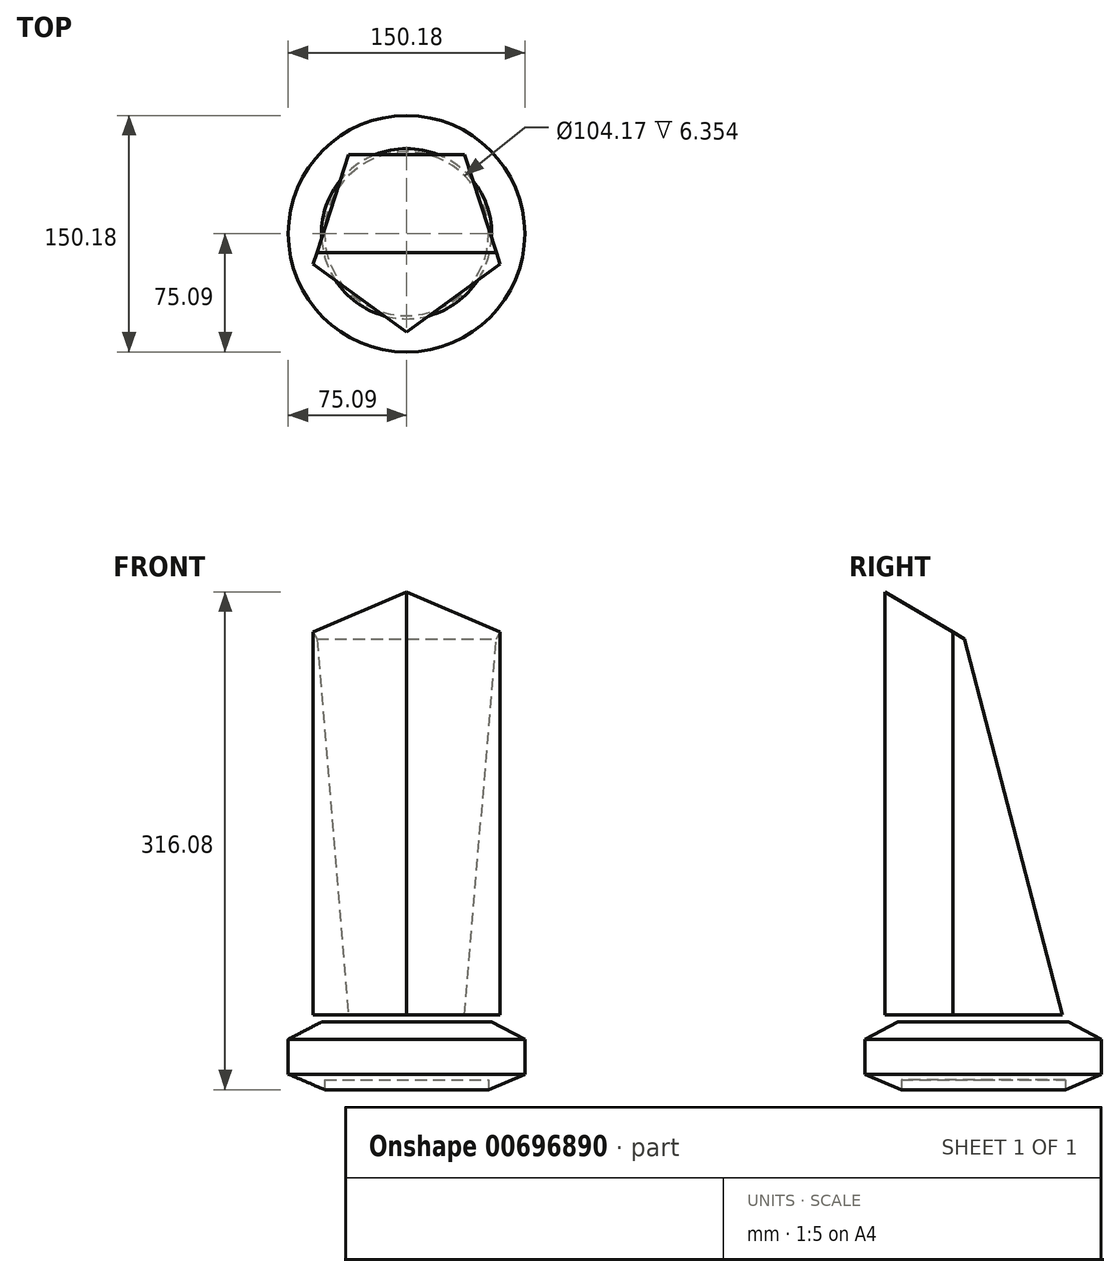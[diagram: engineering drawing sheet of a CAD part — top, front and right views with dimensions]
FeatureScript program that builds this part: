
annotation { "Feature Type Name" : "Feature", "Feature Type Description" : "" }
export const myFeature = defineFeature(function(context is Context, id is Id, definition is map)
    precondition{}
    {
        {
            var Q0;
            Q0=qCreatedBy(makeId("Top.planeOp"),FACE);
            var sketch = newSketch(context, id + "F0", { "sketchPlane" : qUnion([Q0])});
            skCircle(sketch, "E0.cCircle", {"center": v(0, 0) * mm, "radius": 50.53 * mm, "construction": true});
            skLineSegment(sketch, "E0.0", {"start": v(-36.71, 50.53) * mm, "end": v(36.71, 50.53) * mm});
            skLineSegment(sketch, "E0.1", {"start": v(36.71, 50.53) * mm, "end": v(59.4, -19.3) * mm});
            skLineSegment(sketch, "E0.2", {"start": v(59.4, -19.3) * mm, "end": v(0, -62.46) * mm});
            skLineSegment(sketch, "E0.3", {"start": v(0, -62.46) * mm, "end": v(-59.4, -19.3) * mm});
            skLineSegment(sketch, "E0.4", {"start": v(-59.4, -19.3) * mm, "end": v(-36.71, 50.53) * mm});
            skPoint(sketch, "E0.0.midPoint", {"position": v(0, 50.53) * mm});
            skSolve(sketch);
        }
        {
            var Q0;
            Q0=makeQuery(id+"F0.imprint","IMPRINT",FACE,{"disambiguationData":[TD([[makeQuery(id+"F0.imprint","IMPRINT",EDGE,{"derivedFrom":sQuery(id+"F0.wireOp",EDGE,"E0.0")}),-1.0]])]});
            extrude(context, id + "F1", {"entities" : qUnion([Q0]), "depth" : 274.32 * mm, "offsetDistance" : 25.4 * mm});
        }
        {
            var Q0;
            Q0=qCreatedBy(makeId("Right.planeOp"),FACE);
            var sketch = newSketch(context, id + "F2", { "sketchPlane" : qUnion([Q0])});
            skLineSegment(sketch, "E1", {"start": v(110.7, 303.13) * mm, "end": v(53.46, -12.62) * mm});
            skLineSegment(sketch, "E2", {"start": v(53.46, -12.62) * mm, "end": v(-11.84, 238.66) * mm});
            skLineSegment(sketch, "E3", {"start": v(-11.84, 238.66) * mm, "end": v(-68.95, 272.35) * mm});
            skLineSegment(sketch, "E4", {"start": v(-68.95, 272.35) * mm, "end": v(-68.95, 303.13) * mm});
            skLineSegment(sketch, "E5", {"start": v(-68.95, 303.13) * mm, "end": v(110.7, 303.13) * mm});
            skSolve(sketch);
        }
        {
            var Q0;
            Q0 = qSketchRegion(id + "F2", true);
            extrude(context, id + "F3", {"entities" : qUnion([Q0]), "operationType" : NewBodyOperationType.REMOVE, "oppositeDirection" : true, "depth" : 76.2 * mm, "offsetDistance" : 25.4 * mm, "hasSecondDirection" : true, "secondDirectionOppositeDirection" : false, "secondDirectionDepth" : 76.2 * mm});
        }
        {
            var Q0;
            Q0=qCreatedBy(makeId("Front.planeOp"),FACE);
            var sketch = newSketch(context, id + "F4", { "sketchPlane" : qUnion([Q0])});
            skLineSegment(sketch, "E6", {"start": v(0, -29.8) * mm, "end": v(0, -4.6) * mm, "construction": true});
            skLineSegment(sketch, "E7", {"start": v(0, -4.6) * mm, "end": v(-54.06, -4.6) * mm});
            skLineSegment(sketch, "E8", {"start": v(-54.06, -4.6) * mm, "end": v(-75.1, -15.56) * mm});
            skLineSegment(sketch, "E9", {"start": v(-75.1, -15.56) * mm, "end": v(-75.1, -37.7) * mm});
            skLineSegment(sketch, "E10", {"start": v(-75.1, -37.7) * mm, "end": v(-52.09, -47.55) * mm});
            skLineSegment(sketch, "E11", {"start": v(-52.09, -47.55) * mm, "end": v(-52.09, -41.2) * mm});
            skLineSegment(sketch, "E12", {"start": v(-52.09, -41.2) * mm, "end": v(0, -41.2) * mm});
            skLineSegment(sketch, "E13", {"start": v(0, -41.2) * mm, "end": v(0, -4.6) * mm});
            skSolve(sketch);
        }
        {
            var Q0;
            Q0=makeQuery(id+"F4.imprint","IMPRINT",FACE,{"disambiguationData":[TD([[makeQuery(id+"F4.imprint","IMPRINT",EDGE,{"derivedFrom":sQuery(id+"F4.wireOp",EDGE,"E7")}),1.0]])]});
            var Q1;
            Q1=sQuery(id+"F4.wireOp",EDGE,"E13");
            revolve(context, id + "F5", {"entities" : qUnion([Q0]), "axis" : qUnion([Q1]), "revolveType" : RevolveType.FULL});
        }
    });
